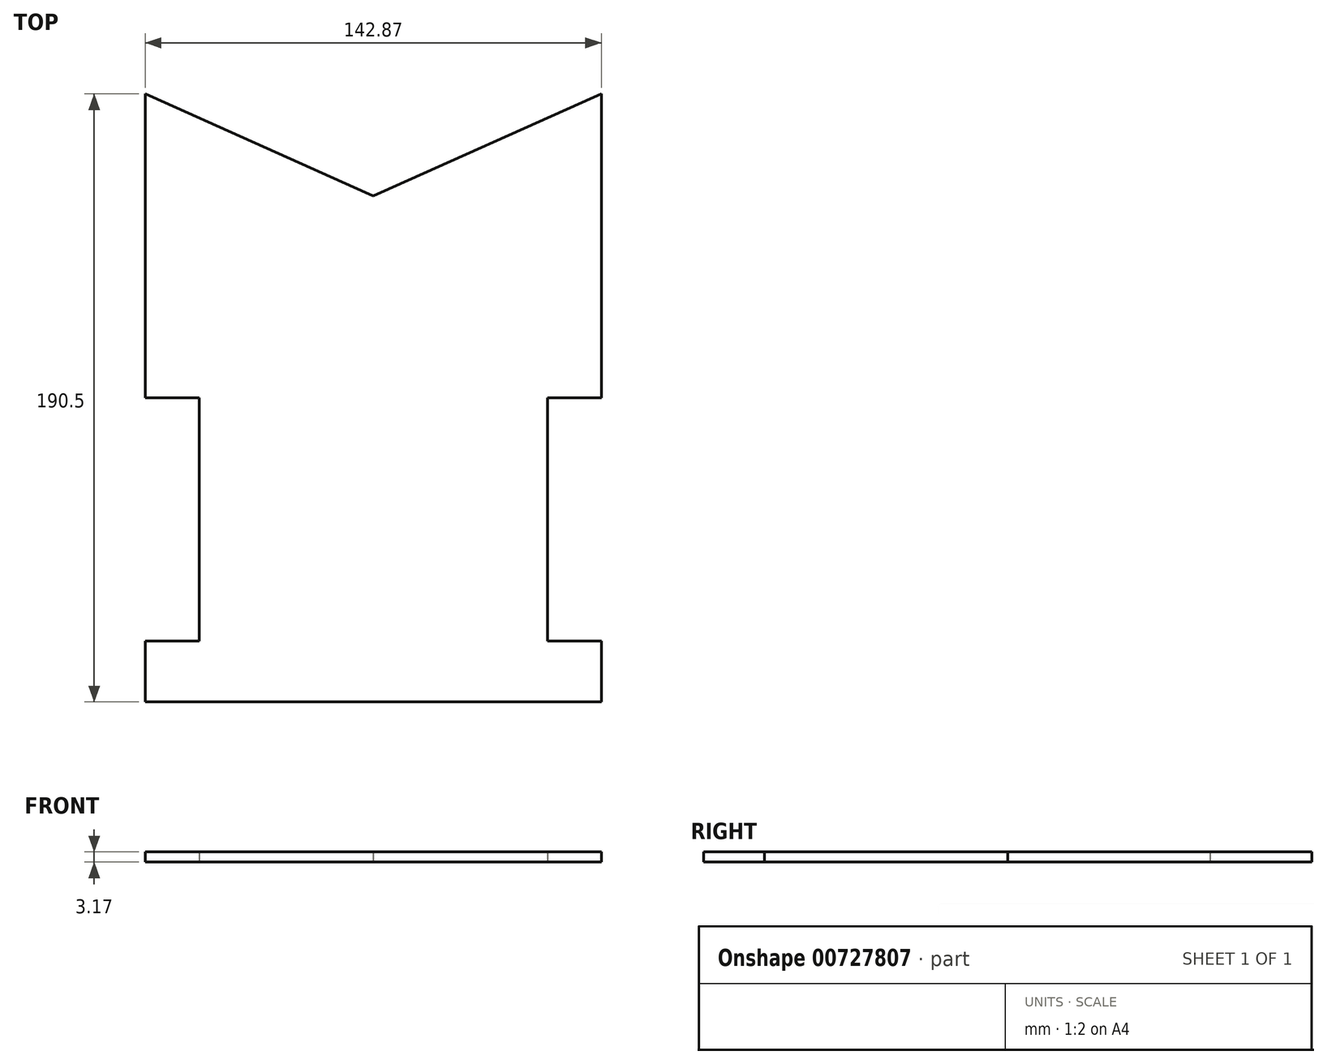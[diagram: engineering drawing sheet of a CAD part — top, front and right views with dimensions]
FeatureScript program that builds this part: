
annotation { "Feature Type Name" : "Feature", "Feature Type Description" : "" }
export const myFeature = defineFeature(function(context is Context, id is Id, definition is map)
    precondition{}
    {
        {
            var Q0;
            Q0=qCreatedBy(makeId("Top.planeOp"),FACE);
            var sketch = newSketch(context, id + "F0", { "sketchPlane" : qUnion([Q0])});
            skLineSegment(sketch, "E0.top", {"start": v(-44.86, -98.3) * mm, "end": v(98.01, -98.3) * mm});
            skLineSegment(sketch, "E0.left", {"start": v(-44.86, 92.2) * mm, "end": v(-44.86, -3.06) * mm});
            skLineSegment(sketch, "E0.right", {"start": v(98.01, 92.2) * mm, "end": v(98.01, -3.06) * mm});
            skLineSegment(sketch, "E1", {"start": v(-44.86, 92.2) * mm, "end": v(26.57, 60.29) * mm});
            skLineSegment(sketch, "E2", {"start": v(26.57, 60.29) * mm, "end": v(98.01, 92.2) * mm});
            skLineSegment(sketch, "E3.bottom", {"start": v(-44.86, -3.06) * mm, "end": v(-27.95, -3.06) * mm});
            skLineSegment(sketch, "E3.top", {"start": v(-44.86, -79.26) * mm, "end": v(-27.95, -79.26) * mm});
            skLineSegment(sketch, "E3.right", {"start": v(-27.95, -3.06) * mm, "end": v(-27.95, -79.26) * mm});
            skLineSegment(sketch, "E4", {"start": v(26.57, 60.29) * mm, "end": v(26.57, -98.3) * mm});
            skLineSegment(sketch, "E5.MirrorCS", {"start": v(81.1, -3.06) * mm, "end": v(81.1, -79.26) * mm});
            skLineSegment(sketch, "E6.MirrorCS", {"start": v(98.01, -79.26) * mm, "end": v(81.1, -79.26) * mm});
            skLineSegment(sketch, "E7.MirrorCS", {"start": v(98.01, -3.06) * mm, "end": v(81.1, -3.06) * mm});
            skLineSegment(sketch, "E8.trimOffspring", {"start": v(98.01, -79.26) * mm, "end": v(98.01, -98.3) * mm});
            skLineSegment(sketch, "E9.trimOffspring", {"start": v(-44.86, -79.26) * mm, "end": v(-44.86, -98.3) * mm});
            skSolve(sketch);
        }
        {
            var Q0;
            Q0 = qSketchRegion(id + "F0", true);
            extrude(context, id + "F1", {"entities" : qUnion([Q0]), "depth" : 3.17 * mm, "offsetDistance" : 25.4 * mm});
        }
    });
